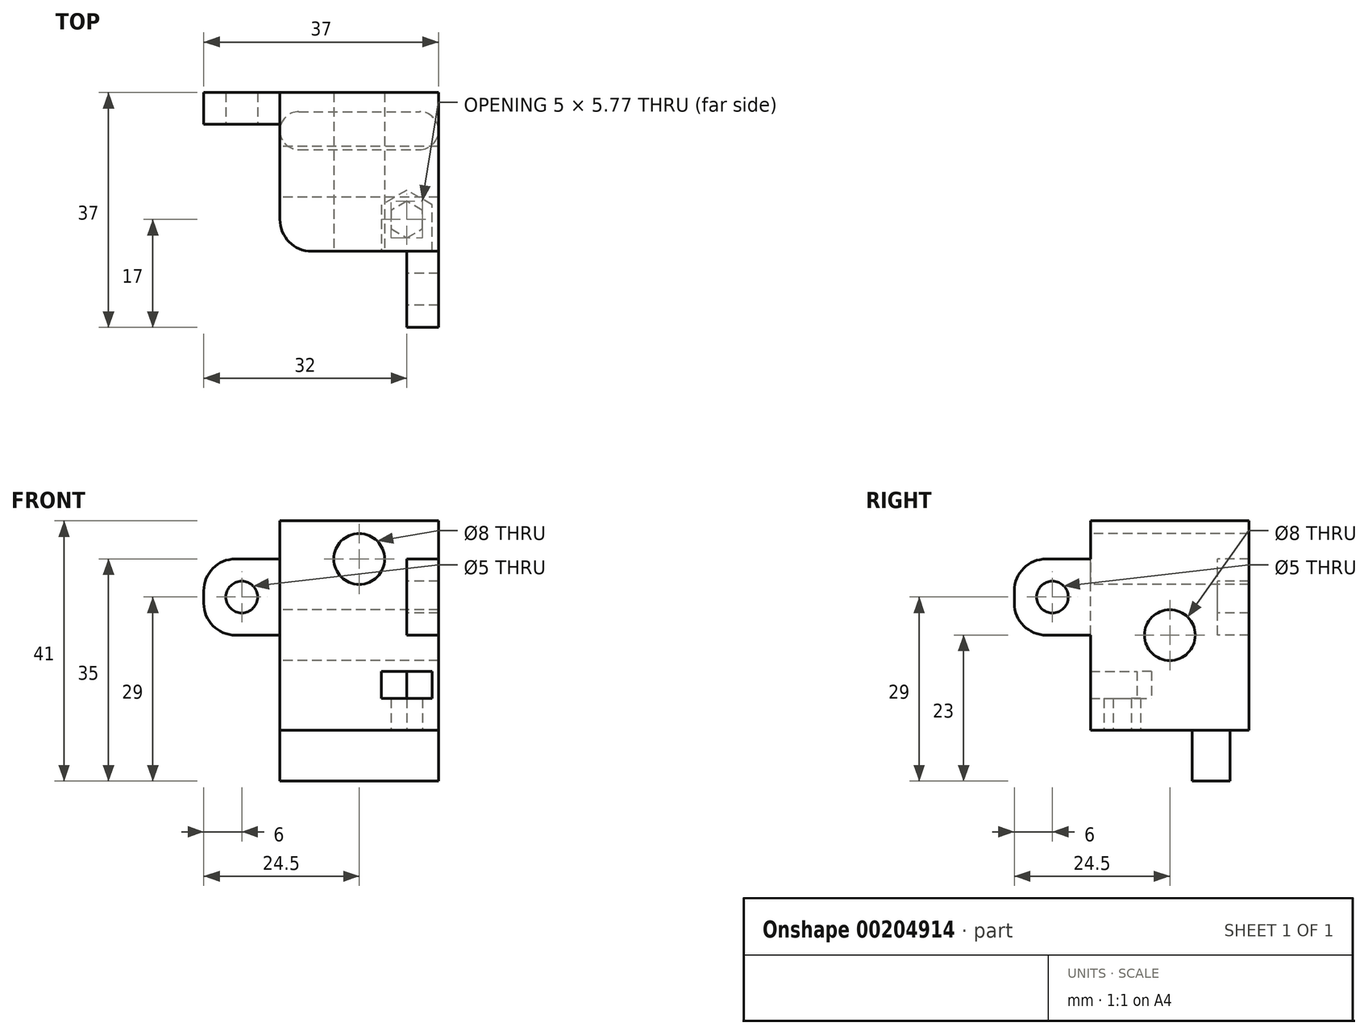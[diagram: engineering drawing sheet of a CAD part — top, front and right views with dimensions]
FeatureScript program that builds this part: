
annotation { "Feature Type Name" : "Feature", "Feature Type Description" : "" }
export const myFeature = defineFeature(function(context is Context, id is Id, definition is map)
    precondition{}
    {
        {
            var Q0;
            Q0=qCreatedBy(makeId("Front.planeOp"),FACE);
            var sketch = newSketch(context, id + "F0", { "sketchPlane" : qUnion([Q0])});
            skLineSegment(sketch, "E0.bottom", {"start": v(0, 0) * mm, "end": v(25, 0) * mm});
            skLineSegment(sketch, "E0.top", {"start": v(0, 45) * mm, "end": v(25, 45) * mm});
            skLineSegment(sketch, "E0.left", {"start": v(0, 0) * mm, "end": v(0, 45) * mm});
            skLineSegment(sketch, "E0.right", {"start": v(25, 0) * mm, "end": v(25, 45) * mm});
            skSolve(sketch);
        }
        {
            var Q0;
            Q0=makeQuery(id+"F0.imprint","IMPRINT",FACE,{"disambiguationData":[TD([[makeQuery(id+"F0.imprint","IMPRINT",EDGE,{"derivedFrom":sQuery(id+"F0.wireOp",EDGE,"E0.bottom")}),1.0]])]});
            extrude(context, id + "F1", {"entities" : qUnion([Q0]), "depth" : 25 * mm});
        }
        {
            var Q0;
            Q0=makeQuery(id+"F1.opExtrude","CAP_FACE",FACE,{"disambiguationData":[OSD([sQuery(id+"F0.wireOp",EDGE,"E0.bottom"),sQuery(id+"F0.wireOp",EDGE,"E0.top"),sQuery(id+"F0.wireOp",EDGE,"E0.left"),sQuery(id+"F0.wireOp",EDGE,"E0.right")])],"isStart":false});
            var sketch = newSketch(context, id + "F2", { "sketchPlane" : qUnion([Q0])});
            skLineSegment(sketch, "E1", {"start": v(12.5, 0) * mm, "end": v(12.5, 37) * mm});
            skCircle(sketch, "E2", {"center": v(12.5, 37) * mm, "radius": 4 * mm});
            skSolve(sketch);
        }
        {
            var Q0;
            Q0=makeQuery(id+"F2.imprint","IMPRINT",FACE,{"disambiguationData":[TD([[makeQuery(id+"F2.imprint","IMPRINT",EDGE,{"derivedFrom":sQuery(id+"F2.wireOp",EDGE,"E2")}),1.0]])]});
            extrude(context, id + "F3", {"entities" : qUnion([Q0]), "operationType" : NewBodyOperationType.REMOVE, "oppositeDirection" : true, "depth" : 25 * mm});
        }
        {
            var Q0;
            Q0=makeQuery(id+"F1.opExtrude","SWEPT_FACE",FACE,{"disambiguationData":[OSD([sQuery(id+"F0.wireOp",EDGE,"E0.left")])]});
            var sketch = newSketch(context, id + "F4", { "sketchPlane" : qUnion([Q0])});
            skLineSegment(sketch, "E3", {"start": v(12.5, 0) * mm, "end": v(12.5, 25) * mm});
            skCircle(sketch, "E4", {"center": v(12.5, 25) * mm, "radius": 4 * mm});
            skSolve(sketch);
        }
        {
            var Q0;
            Q0=makeQuery(id+"F4.imprint","IMPRINT",FACE,{"disambiguationData":[TD([[makeQuery(id+"F4.imprint","IMPRINT",EDGE,{"derivedFrom":sQuery(id+"F4.wireOp",EDGE,"E4")}),1.0]])]});
            extrude(context, id + "F5", {"entities" : qUnion([Q0]), "operationType" : NewBodyOperationType.REMOVE, "oppositeDirection" : true, "depth" : 25 * mm});
        }
        {
            var Q0;
            Q0=makeQuery(id+"F1.opExtrude","SWEPT_FACE",FACE,{"disambiguationData":[OSD([sQuery(id+"F0.wireOp",EDGE,"E0.left")])]});
            var sketch = newSketch(context, id + "F6", { "sketchPlane" : qUnion([Q0])});
            skLineSegment(sketch, "E5.bottom", {"start": v(0, 25) * mm, "end": v(5, 25) * mm});
            skLineSegment(sketch, "E5.top", {"start": v(0, 37) * mm, "end": v(5, 37) * mm});
            skLineSegment(sketch, "E5.left", {"start": v(0, 25) * mm, "end": v(0, 37) * mm});
            skLineSegment(sketch, "E5.right", {"start": v(5, 25) * mm, "end": v(5, 37) * mm});
            skSolve(sketch);
        }
        {
            var Q0;
            Q0=makeQuery(id+"F6.imprint","IMPRINT",FACE,{"disambiguationData":[TD([[makeQuery(id+"F6.imprint","IMPRINT",EDGE,{"derivedFrom":sQuery(id+"F6.wireOp",EDGE,"E5.bottom")}),1.0]])]});
            extrude(context, id + "F7", {"entities" : qUnion([Q0]), "operationType" : NewBodyOperationType.ADD, "depth" : 12 * mm});
        }
        {
            var Q0;
            Q0=makeQuery(id+"F7.opExtrude","SWEPT_FACE",FACE,{"disambiguationData":[OSD([sQuery(id+"F6.wireOp",EDGE,"E5.right")])]});
            var sketch = newSketch(context, id + "F8", { "sketchPlane" : qUnion([Q0])});
            skLineSegment(sketch, "E6", {"start": v(-6, 25) * mm, "end": v(-6, 37) * mm});
            skCircle(sketch, "E7", {"center": v(-6, 31) * mm, "radius": 2.5 * mm});
            skSolve(sketch);
        }
        {
            var Q0;
            {var subQ0=sQuery(id+"F8.wireOp",EDGE,"E7");var subQ1=sQuery(id+"F8.wireOp",EDGE,"E6");var subQ2=makeQuery(id+"F8.imprint","INTERSECT",VERTEX,{"disambiguationData":[OD(0.0)],"derivedFrom":[subQ1,subQ0]});Q0=makeQuery(id+"F8.imprint","IMPRINT",FACE,{"disambiguationData":[TD([[makeQuery(id+"F8.imprint","IMPRINT",EDGE,{"disambiguationData":[TD([[subQ2,-1.0]])],"derivedFrom":subQ1}),1.0]])]});}
            var Q1;
            {var subQ0=sQuery(id+"F8.wireOp",EDGE,"E7");var subQ1=sQuery(id+"F8.wireOp",EDGE,"E6");var subQ2=makeQuery(id+"F8.imprint","INTERSECT",VERTEX,{"disambiguationData":[OD(0.0)],"derivedFrom":[subQ1,subQ0]});Q1=makeQuery(id+"F8.imprint","IMPRINT",FACE,{"disambiguationData":[TD([[makeQuery(id+"F8.imprint","IMPRINT",EDGE,{"disambiguationData":[TD([[subQ2,-1.0]])],"derivedFrom":subQ1}),-1.0]])]});}
            extrude(context, id + "F9", {"entities" : qUnion([Q0, Q1]), "operationType" : NewBodyOperationType.REMOVE, "oppositeDirection" : true, "depth" : 25 * mm});
        }
        {
            var Q0;
            Q0=makeQuery(id+"F7.opExtrude","CAP_EDGE",EDGE,{"disambiguationData":[OSD([sQuery(id+"F6.wireOp",EDGE,"E5.top")])],"isStart":false});
            var Q1;
            Q1=makeQuery(id+"F7.opExtrude","CAP_EDGE",EDGE,{"disambiguationData":[OSD([sQuery(id+"F6.wireOp",EDGE,"E5.bottom")])],"isStart":false});
            var Q2;
            Q2=makeQuery(id+"F7.opExtrude","CAP_EDGE",EDGE,{"disambiguationData":[OSD([sQuery(id+"F6.wireOp",EDGE,"E5.top")])],"isStart":true});
            fillet(context, id + "F10", {"entities" : qUnion([Q0, Q1, Q2]), "radius" : 5 * mm, "tangentPropagation" : true, "allowEdgeOverflow" : false});
        }
        {
            var Q0;
            Q0=makeQuery(id+"F1.opExtrude","CAP_FACE",FACE,{"disambiguationData":[OSD([sQuery(id+"F0.wireOp",EDGE,"E0.bottom"),sQuery(id+"F0.wireOp",EDGE,"E0.top"),sQuery(id+"F0.wireOp",EDGE,"E0.left"),sQuery(id+"F0.wireOp",EDGE,"E0.right")])],"isStart":false});
            var sketch = newSketch(context, id + "F11", { "sketchPlane" : qUnion([Q0])});
            skLineSegment(sketch, "E8.bottom", {"start": v(25, 25) * mm, "end": v(20, 25) * mm});
            skLineSegment(sketch, "E8.top", {"start": v(25, 37) * mm, "end": v(20, 37) * mm});
            skLineSegment(sketch, "E8.left", {"start": v(25, 25) * mm, "end": v(25, 37) * mm});
            skLineSegment(sketch, "E8.right", {"start": v(20, 25) * mm, "end": v(20, 37) * mm});
            skSolve(sketch);
        }
        {
            var Q0;
            Q0=makeQuery(id+"F11.imprint","IMPRINT",FACE,{"disambiguationData":[TD([[makeQuery(id+"F11.imprint","IMPRINT",EDGE,{"derivedFrom":sQuery(id+"F11.wireOp",EDGE,"E8.bottom")}),-1.0]])]});
            extrude(context, id + "F12", {"entities" : qUnion([Q0]), "operationType" : NewBodyOperationType.ADD, "depth" : 12 * mm});
        }
        {
            var Q0;
            Q0=makeQuery(id+"F12.opExtrude","SWEPT_FACE",FACE,{"disambiguationData":[OSD([sQuery(id+"F11.wireOp",EDGE,"E8.right")])]});
            var sketch = newSketch(context, id + "F13", { "sketchPlane" : qUnion([Q0])});
            skLineSegment(sketch, "E9", {"start": v(31, 25) * mm, "end": v(31, 37) * mm});
            skCircle(sketch, "E10", {"center": v(31, 31) * mm, "radius": 2.5 * mm});
            skSolve(sketch);
        }
        {
            var Q0;
            {var subQ0=sQuery(id+"F13.wireOp",EDGE,"E10");var subQ1=sQuery(id+"F13.wireOp",EDGE,"E9");var subQ2=makeQuery(id+"F13.imprint","INTERSECT",VERTEX,{"disambiguationData":[OD(0.0)],"derivedFrom":[subQ1,subQ0]});Q0=makeQuery(id+"F13.imprint","IMPRINT",FACE,{"disambiguationData":[TD([[makeQuery(id+"F13.imprint","IMPRINT",EDGE,{"disambiguationData":[TD([[subQ2,-1.0]])],"derivedFrom":subQ1}),1.0]])]});}
            var Q1;
            {var subQ0=sQuery(id+"F13.wireOp",EDGE,"E10");var subQ1=sQuery(id+"F13.wireOp",EDGE,"E9");var subQ2=makeQuery(id+"F13.imprint","INTERSECT",VERTEX,{"disambiguationData":[OD(0.0)],"derivedFrom":[subQ1,subQ0]});Q1=makeQuery(id+"F13.imprint","IMPRINT",FACE,{"disambiguationData":[TD([[makeQuery(id+"F13.imprint","IMPRINT",EDGE,{"disambiguationData":[TD([[subQ2,-1.0]])],"derivedFrom":subQ1}),-1.0]])]});}
            extrude(context, id + "F14", {"entities" : qUnion([Q0, Q1]), "operationType" : NewBodyOperationType.REMOVE, "oppositeDirection" : true, "depth" : 25 * mm});
        }
        {
            var Q0;
            Q0=makeQuery(id+"F12.opExtrude","CAP_EDGE",EDGE,{"disambiguationData":[OSD([sQuery(id+"F11.wireOp",EDGE,"E8.top")])],"isStart":false});
            var Q1;
            Q1=makeQuery(id+"F12.opExtrude","CAP_EDGE",EDGE,{"disambiguationData":[OSD([sQuery(id+"F11.wireOp",EDGE,"E8.bottom")])],"isStart":false});
            var Q2;
            Q2=makeQuery(id+"F12.opExtrude","CAP_EDGE",EDGE,{"disambiguationData":[OSD([sQuery(id+"F11.wireOp",EDGE,"E8.bottom")])],"isStart":true});
            fillet(context, id + "F15", {"entities" : qUnion([Q0, Q1, Q2]), "radius" : 5 * mm, "tangentPropagation" : true, "allowEdgeOverflow" : false});
        }
        {
            var Q0;
            Q0=makeQuery(id+"F1.opExtrude","SWEPT_FACE",FACE,{"disambiguationData":[OSD([sQuery(id+"F0.wireOp",EDGE,"E0.left")])]});
            var sketch = newSketch(context, id + "F16", { "sketchPlane" : qUnion([Q0])});
            skLineSegment(sketch, "E11.bottom", {"start": v(25, 4) * mm, "end": v(6, 4) * mm});
            skLineSegment(sketch, "E11.top", {"start": v(25, 10) * mm, "end": v(6, 10) * mm});
            skLineSegment(sketch, "E11.left", {"start": v(25, 4) * mm, "end": v(25, 10) * mm});
            skLineSegment(sketch, "E11.right", {"start": v(6, 4) * mm, "end": v(6, 10) * mm});
            skSolve(sketch);
        }
        {
            var Q0;
            Q0=makeQuery(id+"F16.imprint","IMPRINT",FACE,{"disambiguationData":[TD([[makeQuery(id+"F16.imprint","IMPRINT",EDGE,{"derivedFrom":sQuery(id+"F16.wireOp",EDGE,"E11.bottom")}),-1.0]])]});
            extrude(context, id + "F17", {"entities" : qUnion([Q0]), "operationType" : NewBodyOperationType.REMOVE, "oppositeDirection" : true, "depth" : 19 * mm});
        }
        {
            var Q0;
            Q0=makeQuery(id+"F1.opExtrude","SWEPT_FACE",FACE,{"disambiguationData":[OSD([sQuery(id+"F0.wireOp",EDGE,"E0.bottom")])]});
            var sketch = newSketch(context, id + "F18", { "sketchPlane" : qUnion([Q0])});
            skCircle(sketch, "E12.cCircle", {"center": v(20, 20) * mm, "radius": 2.5 * mm, "construction": true});
            skLineSegment(sketch, "E12.0", {"start": v(17.5, 18.56) * mm, "end": v(17.5, 21.44) * mm});
            skLineSegment(sketch, "E12.1", {"start": v(17.5, 21.44) * mm, "end": v(20, 22.89) * mm});
            skLineSegment(sketch, "E12.2", {"start": v(20, 22.89) * mm, "end": v(22.5, 21.44) * mm});
            skLineSegment(sketch, "E12.3", {"start": v(22.5, 21.44) * mm, "end": v(22.5, 18.56) * mm});
            skLineSegment(sketch, "E12.4", {"start": v(22.5, 18.56) * mm, "end": v(20, 17.11) * mm});
            skLineSegment(sketch, "E12.5", {"start": v(20, 17.11) * mm, "end": v(17.5, 18.56) * mm});
            skPoint(sketch, "E12.0.midPoint", {"position": v(17.5, 20) * mm});
            skLineSegment(sketch, "E13", {"start": v(20, 20) * mm, "end": v(20, 25) * mm});
            skLineSegment(sketch, "E14", {"start": v(20, 20) * mm, "end": v(25, 20) * mm});
            skSolve(sketch);
        }
        {
            var Q0;
            {var subQ3=sQuery(id+"F18.wireOp",EDGE,"E12.0");Q0=makeQuery(id+"F18.imprint","IMPRINT",FACE,{"disambiguationData":[TD([[makeQuery(id+"F18.imprint","IMPRINT",EDGE,{"derivedFrom":subQ3}),-1.0]])]});}
            var Q1;
            {var subQ0=sQuery(id+"F18.wireOp",EDGE,"E12.2");Q1=makeQuery(id+"F18.imprint","IMPRINT",FACE,{"disambiguationData":[TD([[makeQuery(id+"F18.imprint","IMPRINT",EDGE,{"derivedFrom":subQ0}),-1.0]])]});}
            extrude(context, id + "F19", {"entities" : qUnion([Q0, Q1]), "operationType" : NewBodyOperationType.REMOVE, "oppositeDirection" : true, "depth" : 12 * mm});
        }
        {
            var Q0;
            Q0=makeQuery(id+"F17.boolean.opBoolean","COPY",EDGE,{"derivedFrom":makeQuery(id+"F17.opExtrude","CAP_EDGE",EDGE,{"disambiguationData":[OSD([sQuery(id+"F16.wireOp",EDGE,"E11.right")])],"isStart":false})});
            fillet(context, id + "F20", {"entities" : qUnion([Q0]), "radius" : 5 * mm, "tangentPropagation" : true, "allowEdgeOverflow" : false});
        }
        {
            var Q0;
            {var subQ0=sQuery(id+"F0.wireOp",EDGE,"E0.bottom");var subQ1=sQuery(id+"F0.wireOp",EDGE,"E0.left");Q0=makeQuery(id+"F17.boolean.opBoolean","SPLIT",EDGE,{"disambiguationData":[TD([makeQuery(id+"F1.opExtrude","SWEPT_FACE",FACE,{"disambiguationData":[OSD([subQ0])]})])],"derivedFrom":makeQuery(id+"F1.opExtrude","CAP_EDGE",EDGE,{"disambiguationData":[OSD([subQ1])],"isStart":false})});}
            var Q1;
            {var subQ0=sQuery(id+"F0.wireOp",EDGE,"E0.left");var subQ1=sQuery(id+"F0.wireOp",EDGE,"E0.top");Q1=makeQuery(id+"F17.boolean.opBoolean","SPLIT",EDGE,{"disambiguationData":[TD([makeQuery(id+"F1.opExtrude","SWEPT_FACE",FACE,{"disambiguationData":[OSD([subQ1])]})])],"derivedFrom":makeQuery(id+"F1.opExtrude","CAP_EDGE",EDGE,{"disambiguationData":[OSD([subQ0])],"isStart":false})});}
            fillet(context, id + "F21", {"entities" : qUnion([Q0, Q1]), "radius" : 5 * mm, "tangentPropagation" : true, "allowEdgeOverflow" : false});
        }
        {
            var Q0;
            Q0=makeQuery(id+"F1.opExtrude","SWEPT_FACE",FACE,{"disambiguationData":[OSD([sQuery(id+"F0.wireOp",EDGE,"E0.top")])]});
            extrude(context, id + "F22", {"entities" : qUnion([Q0]), "operationType" : NewBodyOperationType.REMOVE, "oppositeDirection" : true, "depth" : 2 * mm});
        }
        {
            var Q0;
            Q0=makeQuery(id+"F1.opExtrude","CAP_FACE",FACE,{"disambiguationData":[OSD([sQuery(id+"F0.wireOp",EDGE,"E0.bottom"),sQuery(id+"F0.wireOp",EDGE,"E0.top"),sQuery(id+"F0.wireOp",EDGE,"E0.left"),sQuery(id+"F0.wireOp",EDGE,"E0.right")])],"isStart":false});
            var sketch = newSketch(context, id + "F23", { "sketchPlane" : qUnion([Q0])});
            skLineSegment(sketch, "E15", {"start": v(19, 10) * mm, "end": v(25, 10) * mm});
            skLineSegment(sketch, "E16.bottom", {"start": v(25, 10) * mm, "end": v(0, 10) * mm});
            skLineSegment(sketch, "E16.top", {"start": v(25, 0) * mm, "end": v(0, 0) * mm});
            skLineSegment(sketch, "E16.left", {"start": v(25, 10) * mm, "end": v(25, 0) * mm});
            skLineSegment(sketch, "E16.right", {"start": v(0, 10) * mm, "end": v(0, 0) * mm});
            skSolve(sketch);
        }
        {
            var Q0;
            {var subQ2=sQuery(id+"F23.wireOp",EDGE,"E16.left");Q0=makeQuery(id+"F23.imprint","IMPRINT",FACE,{"disambiguationData":[TD([[makeQuery(id+"F23.imprint","IMPRINT",EDGE,{"derivedFrom":subQ2}),1.0]])]});}
            var Q1;
            {var subQ0=sQuery(id+"F23.wireOp",EDGE,"E16.right");Q1=makeQuery(id+"F23.imprint","IMPRINT",FACE,{"disambiguationData":[TD([[makeQuery(id+"F23.imprint","IMPRINT",EDGE,{"derivedFrom":subQ0}),1.0]])]});}
            extrude(context, id + "F24", {"entities" : qUnion([Q0, Q1]), "operationType" : NewBodyOperationType.REMOVE, "oppositeDirection" : true, "depth" : 25 * mm});
        }
        {
            var Q0;
            Q0=makeQuery(id+"F24.boolean.opBoolean","MERGE",FACE,{"derivedFrom":[makeQuery(id+"F17.boolean.opBoolean","COPY",FACE,{"derivedFrom":makeQuery(id+"F17.opExtrude","SWEPT_FACE",FACE,{"disambiguationData":[OSD([sQuery(id+"F16.wireOp",EDGE,"E11.top")])]})}),makeQuery(id+"F24.opExtrude","SWEPT_FACE",FACE,{"disambiguationData":[OSD([sQuery(id+"F23.wireOp",EDGE,"E16.bottom")])]})]});
            cPlane(context, id + "F25", {"entities" : qUnion([Q0]), "cplaneType" : CPlaneType.OFFSET, "offset" : 5 * mm, "oppositeDirection" : true, "width" : 150 * mm, "height" : 150 * mm});
        }
        {
            var Q0;
            Q0=qCreatedBy(id+"F25.planeOp",FACE);
            var sketch = newSketch(context, id + "F26", { "sketchPlane" : qUnion([Q0])});
            skLineSegment(sketch, "E17", {"start": v(0, 0) * mm, "end": v(25, 0) * mm});
            skLineSegment(sketch, "E18", {"start": v(20, 20) * mm, "end": v(20, 15.06) * mm});
            skLineSegment(sketch, "E19", {"start": v(20, 15.06) * mm, "end": v(20, 24.25) * mm});
            skCircle(sketch, "E20.cCircle", {"center": v(20, 20) * mm, "radius": 4 * mm, "construction": true});
            skLineSegment(sketch, "E20.0", {"start": v(24, 22.3) * mm, "end": v(24, 17.7) * mm});
            skLineSegment(sketch, "E20.1", {"start": v(24, 17.7) * mm, "end": v(20, 15.38) * mm});
            skLineSegment(sketch, "E20.2", {"start": v(20, 15.38) * mm, "end": v(16, 17.7) * mm});
            skLineSegment(sketch, "E20.3", {"start": v(16, 17.7) * mm, "end": v(16, 22.3) * mm});
            skLineSegment(sketch, "E20.4", {"start": v(16, 22.3) * mm, "end": v(20, 24.62) * mm});
            skLineSegment(sketch, "E20.5", {"start": v(20, 24.62) * mm, "end": v(24, 22.3) * mm});
            skPoint(sketch, "E20.0.midPoint", {"position": v(24, 20) * mm});
            skLineSegment(sketch, "E21", {"start": v(16, 22.3) * mm, "end": v(16, 30.3) * mm});
            skLineSegment(sketch, "E22", {"start": v(16, 30.3) * mm, "end": v(24, 30.3) * mm});
            skLineSegment(sketch, "E23", {"start": v(24, 30.3) * mm, "end": v(24, 22.3) * mm});
            skSolve(sketch);
        }
        {
            var Q0;
            Q0 = qSketchRegion(id + "F26", true);
            extrude(context, id + "F27", {"entities" : qUnion([Q0]), "operationType" : NewBodyOperationType.REMOVE, "oppositeDirection" : true, "depth" : 4.3 * mm});
        }
        {
            var Q0;
            Q0=makeQuery(id+"F19.boolean.opBoolean","COPY",FACE,{"derivedFrom":makeQuery(id+"F19.opExtrude","CAP_FACE",FACE,{"disambiguationData":[OSD([sQuery(id+"F18.wireOp",EDGE,"E12.0"),sQuery(id+"F18.wireOp",EDGE,"E12.1"),sQuery(id+"F18.wireOp",EDGE,"E12.2"),sQuery(id+"F18.wireOp",EDGE,"E12.3"),sQuery(id+"F18.wireOp",EDGE,"E12.4"),sQuery(id+"F18.wireOp",EDGE,"E12.5")])],"isStart":false})});
            extrude(context, id + "F28", {"entities" : qUnion([Q0]), "operationType" : NewBodyOperationType.REMOVE, "oppositeDirection" : true, "depth" : 5 * mm});
        }
        {
            var Q0;
            Q0=makeQuery(id+"F24.boolean.opBoolean","MERGE",FACE,{"derivedFrom":[makeQuery(id+"F17.boolean.opBoolean","COPY",FACE,{"derivedFrom":makeQuery(id+"F17.opExtrude","SWEPT_FACE",FACE,{"disambiguationData":[OSD([sQuery(id+"F16.wireOp",EDGE,"E11.top")])]})}),makeQuery(id+"F24.opExtrude","SWEPT_FACE",FACE,{"disambiguationData":[OSD([sQuery(id+"F23.wireOp",EDGE,"E16.bottom")])]})]});
            var sketch = newSketch(context, id + "F29", { "sketchPlane" : qUnion([Q0])});
            skLineSegment(sketch, "E24.bottom", {"start": v(3, 3) * mm, "end": v(22, 3) * mm});
            skLineSegment(sketch, "E24.top", {"start": v(3, 9) * mm, "end": v(22, 9) * mm});
            skLineSegment(sketch, "E24.left", {"start": v(0, 6) * mm, "end": v(0, 6) * mm});
            skLineSegment(sketch, "E24.right", {"start": v(25, 6) * mm, "end": v(25, 6) * mm});
            skPoint(sketch, "E25.visualSharp", {"position": v(0, 3) * mm});
            skArc(sketch, "E25.filletArc", {"start": v(0, 6) * mm, "mid": v(0.88, 3.88) * mm, "end": v(3, 3) * mm});
            skPoint(sketch, "E26.visualSharp", {"position": v(0, 9) * mm});
            skArc(sketch, "E26.filletArc", {"start": v(3, 9) * mm, "mid": v(0.88, 8.12) * mm, "end": v(0, 6) * mm});
            skPoint(sketch, "E27.visualSharp", {"position": v(25, 9) * mm});
            skArc(sketch, "E27.filletArc", {"start": v(25, 6) * mm, "mid": v(24.12, 8.12) * mm, "end": v(22, 9) * mm});
            skPoint(sketch, "E28.visualSharp", {"position": v(25, 3) * mm});
            skArc(sketch, "E28.filletArc", {"start": v(22, 3) * mm, "mid": v(24.12, 3.88) * mm, "end": v(25, 6) * mm});
            skSolve(sketch);
        }
        {
            var Q0;
            Q0=makeQuery(id+"F29.imprint","IMPRINT",FACE,{"disambiguationData":[TD([[makeQuery(id+"F29.imprint","IMPRINT",EDGE,{"derivedFrom":sQuery(id+"F29.wireOp",EDGE,"E24.bottom")}),1.0]])]});
            extrude(context, id + "F30", {"entities" : qUnion([Q0]), "operationType" : NewBodyOperationType.ADD, "depth" : 8 * mm});
        }
    });
